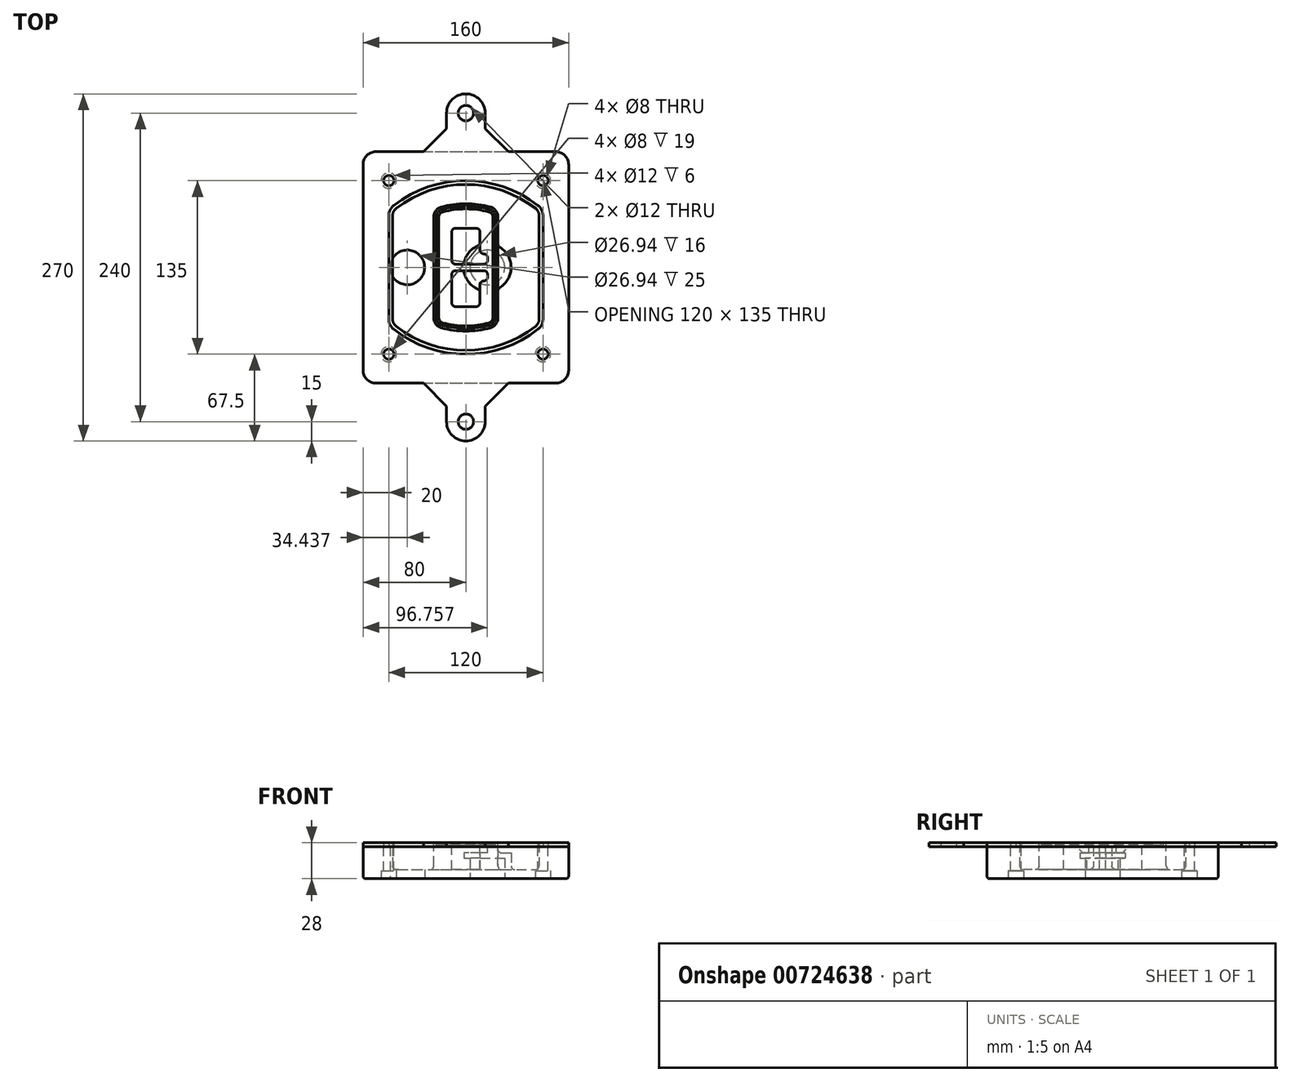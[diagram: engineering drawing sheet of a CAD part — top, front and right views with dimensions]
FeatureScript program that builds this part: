
annotation { "Feature Type Name" : "Feature", "Feature Type Description" : "" }
export const myFeature = defineFeature(function(context is Context, id is Id, definition is map)
    precondition{}
    {
        {
            var Q0;
            Q0=qCreatedBy(makeId("Top.planeOp"),FACE);
            var sketch = newSketch(context, id + "F0", { "sketchPlane" : qUnion([Q0])});
            skPoint(sketch, "E0.rect.middle", {"position": v(0, 0) * mm});
            skLineSegment(sketch, "E1.bottom", {"start": v(-70, -90) * mm, "end": v(70, -90) * mm});
            skLineSegment(sketch, "E1.top", {"start": v(-70, 90) * mm, "end": v(70, 90) * mm});
            skLineSegment(sketch, "E1.left", {"start": v(-80, -80) * mm, "end": v(-80, 80) * mm});
            skLineSegment(sketch, "E1.right", {"start": v(80, -80) * mm, "end": v(80, 80) * mm});
            skLineSegment(sketch, "E2", {"start": v(-80, 90) * mm, "end": v(80, -90) * mm, "construction": true});
            skLineSegment(sketch, "E3", {"start": v(80, 90) * mm, "end": v(-80, -90) * mm, "construction": true});
            skCircle(sketch, "E4", {"center": v(-60, 67.5) * mm, "radius": 4 * mm});
            skCircle(sketch, "E5", {"center": v(60, 67.5) * mm, "radius": 4 * mm});
            skCircle(sketch, "E6", {"center": v(60, -67.5) * mm, "radius": 4 * mm});
            skCircle(sketch, "E7", {"center": v(-60, -67.5) * mm, "radius": 4 * mm});
            skLineSegment(sketch, "E8", {"start": v(-60, 67.5) * mm, "end": v(60, 67.5) * mm, "construction": true});
            skLineSegment(sketch, "E9", {"start": v(60, 67.5) * mm, "end": v(60, -67.5) * mm, "construction": true});
            skLineSegment(sketch, "E10", {"start": v(60, -67.5) * mm, "end": v(-60, -67.5) * mm, "construction": true});
            skLineSegment(sketch, "E11", {"start": v(-60, -67.5) * mm, "end": v(-60, 67.5) * mm, "construction": true});
            skLineSegment(sketch, "E12", {"start": v(-60, 40.3) * mm, "end": v(-60, -40.3) * mm});
            skLineSegment(sketch, "E13", {"start": v(60, 40.3) * mm, "end": v(60, -40.3) * mm});
            skArc(sketch, "E14", {"start": v(56.15, 48.18) * mm, "mid": v(0, 67.5) * mm, "end": v(-56.15, 48.18) * mm});
            skArc(sketch, "E15", {"start": v(-56.15, -48.18) * mm, "mid": v(0, -67.5) * mm, "end": v(56.15, -48.18) * mm});
            skLineSegment(sketch, "E16", {"start": v(-60, 0) * mm, "end": v(60, 0) * mm, "construction": true});
            skPoint(sketch, "E17.visualSharp", {"position": v(-60, -45) * mm});
            skArc(sketch, "E17.filletArc", {"start": v(-60, -40.3) * mm, "mid": v(-58.99, -44.68) * mm, "end": v(-56.15, -48.18) * mm});
            skPoint(sketch, "E18.visualSharp", {"position": v(-60, 45) * mm});
            skArc(sketch, "E18.filletArc", {"start": v(-56.15, 48.18) * mm, "mid": v(-58.99, 44.68) * mm, "end": v(-60, 40.3) * mm});
            skPoint(sketch, "E19.visualSharp", {"position": v(60, 45) * mm});
            skArc(sketch, "E19.filletArc", {"start": v(60, 40.3) * mm, "mid": v(58.99, 44.68) * mm, "end": v(56.15, 48.18) * mm});
            skPoint(sketch, "E20.visualSharp", {"position": v(60, -45) * mm});
            skArc(sketch, "E20.filletArc", {"start": v(56.15, -48.18) * mm, "mid": v(58.99, -44.68) * mm, "end": v(60, -40.3) * mm});
            skPoint(sketch, "E21.visualSharp", {"position": v(-80, 90) * mm});
            skArc(sketch, "E21.filletArc", {"start": v(-70, 90) * mm, "mid": v(-77.07, 87.07) * mm, "end": v(-80, 80) * mm});
            skPoint(sketch, "E22.visualSharp", {"position": v(80, 90) * mm});
            skArc(sketch, "E22.filletArc", {"start": v(80, 80) * mm, "mid": v(77.07, 87.07) * mm, "end": v(70, 90) * mm});
            skPoint(sketch, "E23.visualSharp", {"position": v(80, -90) * mm});
            skArc(sketch, "E23.filletArc", {"start": v(70, -90) * mm, "mid": v(77.07, -87.07) * mm, "end": v(80, -80) * mm});
            skPoint(sketch, "E24.visualSharp", {"position": v(-80, -90) * mm});
            skArc(sketch, "E24.filletArc", {"start": v(-80, -80) * mm, "mid": v(-77.07, -87.07) * mm, "end": v(-70, -90) * mm});
            skArc(sketch, "E25.0", {"start": v(57, 40.3) * mm, "mid": v(56.3, 43.36) * mm, "end": v(54.3, 45.81) * mm});
            skLineSegment(sketch, "E25.1", {"start": v(57, 40.3) * mm, "end": v(57, -40.3) * mm});
            skArc(sketch, "E25.2", {"start": v(54.3, -45.81) * mm, "mid": v(56.3, -43.36) * mm, "end": v(57, -40.3) * mm});
            skArc(sketch, "E25.3", {"start": v(-54.3, -45.81) * mm, "mid": v(0, -64.5) * mm, "end": v(54.3, -45.81) * mm});
            skArc(sketch, "E25.4", {"start": v(-57, -40.3) * mm, "mid": v(-56.3, -43.36) * mm, "end": v(-54.3, -45.81) * mm});
            skArc(sketch, "E25.5", {"start": v(54.3, 45.81) * mm, "mid": v(0, 64.5) * mm, "end": v(-54.3, 45.81) * mm});
            skLineSegment(sketch, "E25.6", {"start": v(-57, 40.3) * mm, "end": v(-57, -40.3) * mm});
            skArc(sketch, "E25.7", {"start": v(-54.3, 45.81) * mm, "mid": v(-56.3, 43.36) * mm, "end": v(-57, 40.3) * mm});
            skArc(sketch, "E26.0", {"start": v(-58.62, 51.33) * mm, "mid": v(-62.58, 46.43) * mm, "end": v(-64, 40.3) * mm});
            skArc(sketch, "E26.1", {"start": v(58.62, 51.33) * mm, "mid": v(0, 71.5) * mm, "end": v(-58.62, 51.33) * mm});
            skArc(sketch, "E26.2", {"start": v(64, 40.3) * mm, "mid": v(62.58, 46.43) * mm, "end": v(58.62, 51.33) * mm});
            skLineSegment(sketch, "E26.3", {"start": v(64, 40.3) * mm, "end": v(64, -40.3) * mm});
            skArc(sketch, "E26.4", {"start": v(58.62, -51.33) * mm, "mid": v(62.58, -46.43) * mm, "end": v(64, -40.3) * mm});
            skLineSegment(sketch, "E26.5", {"start": v(-64, 40.3) * mm, "end": v(-64, -40.3) * mm});
            skArc(sketch, "E26.6", {"start": v(-58.62, -51.33) * mm, "mid": v(0, -71.5) * mm, "end": v(58.62, -51.33) * mm});
            skArc(sketch, "E26.7", {"start": v(-64, -40.3) * mm, "mid": v(-62.58, -46.43) * mm, "end": v(-58.62, -51.33) * mm});
            skSolve(sketch);
        }
        {
            var Q0;
            Q0=makeQuery(id+"F0.imprint","IMPRINT",FACE,{"disambiguationData":[TD([[makeQuery(id+"F0.imprint","IMPRINT",EDGE,{"derivedFrom":sQuery(id+"F0.wireOp",EDGE,"E1.bottom")}),1.0]])]});
            var Q1;
            Q1=makeQuery(id+"F0.imprint","IMPRINT",FACE,{"disambiguationData":[TD([[makeQuery(id+"F0.imprint","IMPRINT",EDGE,{"derivedFrom":sQuery(id+"F0.wireOp",EDGE,"E12")}),1.0]])]});
            var Q2;
            Q2=makeQuery(id+"F0.imprint","IMPRINT",FACE,{"disambiguationData":[TD([[makeQuery(id+"F0.imprint","IMPRINT",EDGE,{"derivedFrom":sQuery(id+"F0.wireOp",EDGE,"E25.0")}),1.0]])]});
            var Q3;
            Q3=makeQuery(id+"F0.imprint","IMPRINT",FACE,{"disambiguationData":[TD([[makeQuery(id+"F0.imprint","IMPRINT",EDGE,{"derivedFrom":sQuery(id+"F0.wireOp",EDGE,"E12")}),-1.0]])]});
            extrude(context, id + "F1", {"entities" : qUnion([Q0, Q1, Q2, Q3]), "oppositeDirection" : true, "depth" : 25 * mm});
        }
        {
            var Q0;
            Q0=makeQuery(id+"F0.imprint","IMPRINT",FACE,{"disambiguationData":[TD([[makeQuery(id+"F0.imprint","IMPRINT",EDGE,{"derivedFrom":sQuery(id+"F0.wireOp",EDGE,"E12")}),1.0]])]});
            extrude(context, id + "F2", {"entities" : qUnion([Q0]), "operationType" : NewBodyOperationType.ADD, "depth" : 3 * mm});
        }
        {
            var Q0;
            Q0=makeQuery(id+"F0.imprint","IMPRINT",FACE,{"disambiguationData":[TD([[makeQuery(id+"F0.imprint","IMPRINT",EDGE,{"derivedFrom":sQuery(id+"F0.wireOp",EDGE,"E25.0")}),1.0]])]});
            extrude(context, id + "F3", {"entities" : qUnion([Q0]), "operationType" : NewBodyOperationType.REMOVE, "oppositeDirection" : true, "depth" : 18 * mm});
        }
        {
            var Q0;
            Q0=makeQuery(id+"F2.opExtrude","CAP_FACE",FACE,{"disambiguationData":[OSD([sQuery(id+"F0.wireOp",EDGE,"E12"),sQuery(id+"F0.wireOp",EDGE,"E13"),sQuery(id+"F0.wireOp",EDGE,"E14"),sQuery(id+"F0.wireOp",EDGE,"E15"),sQuery(id+"F0.wireOp",EDGE,"E17.filletArc"),sQuery(id+"F0.wireOp",EDGE,"E18.filletArc"),sQuery(id+"F0.wireOp",EDGE,"E19.filletArc"),sQuery(id+"F0.wireOp",EDGE,"E20.filletArc"),sQuery(id+"F0.wireOp",EDGE,"E25.0"),sQuery(id+"F0.wireOp",EDGE,"E25.1"),sQuery(id+"F0.wireOp",EDGE,"E25.2"),sQuery(id+"F0.wireOp",EDGE,"E25.3"),sQuery(id+"F0.wireOp",EDGE,"E25.4"),sQuery(id+"F0.wireOp",EDGE,"E25.5"),sQuery(id+"F0.wireOp",EDGE,"E25.6"),sQuery(id+"F0.wireOp",EDGE,"E25.7")])],"isStart":false});
            var sketch = newSketch(context, id + "F4", { "sketchPlane" : qUnion([Q0])});
            skArc(sketch, "E27.0", {"start": v(-19.08, -46.97) * mm, "mid": v(0, -49.5) * mm, "end": v(19.08, -46.97) * mm});
            skArc(sketch, "E28.0", {"start": v(19.08, 46.97) * mm, "mid": v(0, 49.5) * mm, "end": v(-19.08, 46.97) * mm});
            skLineSegment(sketch, "E29", {"start": v(-25, 39.25) * mm, "end": v(-25, -39.25) * mm});
            skLineSegment(sketch, "E30", {"start": v(25, 39.25) * mm, "end": v(25, -39.25) * mm});
            skLineSegment(sketch, "E31", {"start": v(-25, 45.1) * mm, "end": v(25, 45.1) * mm, "construction": true});
            skLineSegment(sketch, "E32", {"start": v(-25, -45.1) * mm, "end": v(25, -45.1) * mm, "construction": true});
            skPoint(sketch, "E33.visualSharp", {"position": v(-25, 45.1) * mm});
            skArc(sketch, "E33.filletArc", {"start": v(-19.08, 46.97) * mm, "mid": v(-23.35, 44.11) * mm, "end": v(-25, 39.25) * mm});
            skPoint(sketch, "E34.visualSharp", {"position": v(25, 45.1) * mm});
            skArc(sketch, "E34.filletArc", {"start": v(25, 39.25) * mm, "mid": v(23.35, 44.11) * mm, "end": v(19.08, 46.97) * mm});
            skPoint(sketch, "E35.visualSharp", {"position": v(25, -45.1) * mm});
            skArc(sketch, "E35.filletArc", {"start": v(19.08, -46.97) * mm, "mid": v(23.35, -44.11) * mm, "end": v(25, -39.25) * mm});
            skPoint(sketch, "E36.visualSharp", {"position": v(-25, -45.1) * mm});
            skArc(sketch, "E36.filletArc", {"start": v(-25, -39.25) * mm, "mid": v(-23.35, -44.11) * mm, "end": v(-19.08, -46.97) * mm});
            skArc(sketch, "E37.0", {"start": v(54.3, 45.81) * mm, "mid": v(0, 64.5) * mm, "end": v(-54.3, 45.81) * mm});
            skArc(sketch, "E37.1", {"start": v(-54.3, 45.81) * mm, "mid": v(-56.3, 43.36) * mm, "end": v(-57, 40.3) * mm});
            skLineSegment(sketch, "E37.2", {"start": v(-57, 40.3) * mm, "end": v(-57, -40.3) * mm});
            skArc(sketch, "E37.3", {"start": v(-57, -40.3) * mm, "mid": v(-56.3, -43.36) * mm, "end": v(-54.3, -45.81) * mm});
            skArc(sketch, "E37.4", {"start": v(-54.3, -45.81) * mm, "mid": v(0, -64.5) * mm, "end": v(54.3, -45.81) * mm});
            skArc(sketch, "E37.5", {"start": v(54.3, -45.81) * mm, "mid": v(56.3, -43.36) * mm, "end": v(57, -40.3) * mm});
            skLineSegment(sketch, "E37.6", {"start": v(57, 40.3) * mm, "end": v(57, -40.3) * mm});
            skArc(sketch, "E37.7", {"start": v(57, 40.3) * mm, "mid": v(56.3, 43.36) * mm, "end": v(54.3, 45.81) * mm});
            skLineSegment(sketch, "E38.0", {"start": v(23, 39.25) * mm, "end": v(23, -39.25) * mm});
            skArc(sketch, "E38.1", {"start": v(18.56, -45.04) * mm, "mid": v(21.76, -42.9) * mm, "end": v(23, -39.25) * mm});
            skArc(sketch, "E38.2", {"start": v(-18.56, -45.04) * mm, "mid": v(0, -47.5) * mm, "end": v(18.56, -45.04) * mm});
            skArc(sketch, "E38.3", {"start": v(-23, -39.25) * mm, "mid": v(-21.76, -42.9) * mm, "end": v(-18.56, -45.04) * mm});
            skLineSegment(sketch, "E38.4", {"start": v(-23, 39.25) * mm, "end": v(-23, -39.25) * mm});
            skArc(sketch, "E38.5", {"start": v(23, 39.25) * mm, "mid": v(21.76, 42.9) * mm, "end": v(18.56, 45.04) * mm});
            skArc(sketch, "E38.6", {"start": v(-18.56, 45.04) * mm, "mid": v(-21.76, 42.9) * mm, "end": v(-23, 39.25) * mm});
            skArc(sketch, "E38.7", {"start": v(18.56, 45.04) * mm, "mid": v(0, 47.5) * mm, "end": v(-18.56, 45.04) * mm});
            skArc(sketch, "E39.0", {"start": v(21, 39.25) * mm, "mid": v(20.18, 41.68) * mm, "end": v(18.04, 43.1) * mm});
            skLineSegment(sketch, "E39.1", {"start": v(21, 39.25) * mm, "end": v(21, -39.25) * mm});
            skArc(sketch, "E39.2", {"start": v(18.04, -43.1) * mm, "mid": v(20.18, -41.68) * mm, "end": v(21, -39.25) * mm});
            skArc(sketch, "E39.3", {"start": v(-18.04, -43.1) * mm, "mid": v(0, -45.5) * mm, "end": v(18.04, -43.1) * mm});
            skArc(sketch, "E39.4", {"start": v(-21, -39.25) * mm, "mid": v(-20.18, -41.68) * mm, "end": v(-18.04, -43.1) * mm});
            skArc(sketch, "E39.5", {"start": v(18.04, 43.1) * mm, "mid": v(0, 45.5) * mm, "end": v(-18.04, 43.1) * mm});
            skLineSegment(sketch, "E39.6", {"start": v(-21, 39.25) * mm, "end": v(-21, -39.25) * mm});
            skArc(sketch, "E39.7", {"start": v(-18.04, 43.1) * mm, "mid": v(-20.18, 41.68) * mm, "end": v(-21, 39.25) * mm});
            skLineSegment(sketch, "E40", {"start": v(-25, 0) * mm, "end": v(25, 0) * mm, "construction": true});
            skLineSegment(sketch, "E41", {"start": v(-11, 5.5) * mm, "end": v(-11, 27.5) * mm});
            skLineSegment(sketch, "E42", {"start": v(-8, 30.5) * mm, "end": v(8, 30.5) * mm});
            skLineSegment(sketch, "E43", {"start": v(11, 27.5) * mm, "end": v(11, 13.5) * mm});
            skLineSegment(sketch, "E44", {"start": v(14, 10.5) * mm, "end": v(14, 10.5) * mm});
            skLineSegment(sketch, "E45", {"start": v(17, 7.5) * mm, "end": v(17, 5.5) * mm});
            skLineSegment(sketch, "E46", {"start": v(14, 2.5) * mm, "end": v(-8, 2.5) * mm});
            skPoint(sketch, "E47.visualSharp", {"position": v(-11, 30.5) * mm});
            skArc(sketch, "E47.filletArc", {"start": v(-8, 30.5) * mm, "mid": v(-10.12, 29.62) * mm, "end": v(-11, 27.5) * mm});
            skPoint(sketch, "E48.visualSharp", {"position": v(11, 30.5) * mm});
            skArc(sketch, "E48.filletArc", {"start": v(11, 27.5) * mm, "mid": v(10.12, 29.62) * mm, "end": v(8, 30.5) * mm});
            skPoint(sketch, "E49.visualSharp", {"position": v(11, 10.5) * mm});
            skArc(sketch, "E49.filletArc", {"start": v(11, 13.5) * mm, "mid": v(11.88, 11.38) * mm, "end": v(14, 10.5) * mm});
            skPoint(sketch, "E50.visualSharp", {"position": v(17, 10.5) * mm});
            skArc(sketch, "E50.filletArc", {"start": v(17, 7.5) * mm, "mid": v(16.12, 9.62) * mm, "end": v(14, 10.5) * mm});
            skPoint(sketch, "E51.visualSharp", {"position": v(17, 2.5) * mm});
            skArc(sketch, "E51.filletArc", {"start": v(14, 2.5) * mm, "mid": v(16.12, 3.38) * mm, "end": v(17, 5.5) * mm});
            skPoint(sketch, "E52.visualSharp", {"position": v(-11, 2.5) * mm});
            skArc(sketch, "E52.filletArc", {"start": v(-11, 5.5) * mm, "mid": v(-10.12, 3.38) * mm, "end": v(-8, 2.5) * mm});
            skLineSegment(sketch, "E53.0.MirrorCS", {"start": v(14, -2.5) * mm, "end": v(-8, -2.5) * mm});
            skArc(sketch, "E54.0.MirrorCS", {"start": v(-11, -5.5) * mm, "mid": v(-10.12, -3.38) * mm, "end": v(-8, -2.5) * mm});
            skLineSegment(sketch, "E55.0.MirrorCS", {"start": v(-11, -5.5) * mm, "end": v(-11, -27.5) * mm});
            skArc(sketch, "E56.0.MirrorCS", {"start": v(-8, -30.5) * mm, "mid": v(-10.12, -29.62) * mm, "end": v(-11, -27.5) * mm});
            skLineSegment(sketch, "E57.0.MirrorCS", {"start": v(-8, -30.5) * mm, "end": v(8, -30.5) * mm});
            skArc(sketch, "E58.0.MirrorCS", {"start": v(11, -27.5) * mm, "mid": v(10.12, -29.62) * mm, "end": v(8, -30.5) * mm});
            skLineSegment(sketch, "E59.0.MirrorCS", {"start": v(11, -27.5) * mm, "end": v(11, -13.5) * mm});
            skArc(sketch, "E60.0.MirrorCS", {"start": v(11, -13.5) * mm, "mid": v(11.88, -11.38) * mm, "end": v(14, -10.5) * mm});
            skArc(sketch, "E61.0.MirrorCS", {"start": v(17, -7.5) * mm, "mid": v(16.12, -9.62) * mm, "end": v(14, -10.5) * mm});
            skLineSegment(sketch, "E62.0.MirrorCS", {"start": v(17, -7.5) * mm, "end": v(17, -5.5) * mm});
            skArc(sketch, "E63.0.MirrorCS", {"start": v(14, -2.5) * mm, "mid": v(16.12, -3.38) * mm, "end": v(17, -5.5) * mm});
            skSolve(sketch);
        }
        {
            var Q0;
            Q0=makeQuery(id+"F4.imprint","IMPRINT",FACE,{"disambiguationData":[TD([[makeQuery(id+"F4.imprint","IMPRINT",EDGE,{"derivedFrom":sQuery(id+"F4.wireOp",EDGE,"E27.0")}),1.0]])]});
            var Q1;
            Q1=makeQuery(id+"F4.imprint","IMPRINT",FACE,{"disambiguationData":[TD([[makeQuery(id+"F4.imprint","IMPRINT",EDGE,{"derivedFrom":sQuery(id+"F4.wireOp",EDGE,"E38.0")}),-1.0]])]});
            var Q2;
            Q2=makeQuery(id+"F4.imprint","IMPRINT",FACE,{"disambiguationData":[TD([[makeQuery(id+"F4.imprint","IMPRINT",EDGE,{"derivedFrom":sQuery(id+"F4.wireOp",EDGE,"E39.0")}),1.0]])]});
            extrude(context, id + "F5", {"entities" : qUnion([Q0, Q1, Q2]), "operationType" : NewBodyOperationType.ADD, "endBound" : BoundingType.UP_TO_NEXT, "oppositeDirection" : true, "depth" : 25 * mm});
        }
        {
            var Q0;
            Q0=makeQuery(id+"F4.imprint","IMPRINT",FACE,{"disambiguationData":[TD([[makeQuery(id+"F4.imprint","IMPRINT",EDGE,{"derivedFrom":sQuery(id+"F4.wireOp",EDGE,"E38.0")}),-1.0]])]});
            extrude(context, id + "F6", {"entities" : qUnion([Q0]), "operationType" : NewBodyOperationType.REMOVE, "oppositeDirection" : true, "depth" : 2 * mm});
        }
        {
            var Q0;
            Q0=makeQuery(id+"F1.opExtrude","CAP_FACE",FACE,{"disambiguationData":[OSD([sQuery(id+"F0.wireOp",EDGE,"E1.bottom"),sQuery(id+"F0.wireOp",EDGE,"E1.top"),sQuery(id+"F0.wireOp",EDGE,"E1.left"),sQuery(id+"F0.wireOp",EDGE,"E1.right"),sQuery(id+"F0.wireOp",EDGE,"E4"),sQuery(id+"F0.wireOp",EDGE,"E5"),sQuery(id+"F0.wireOp",EDGE,"E6"),sQuery(id+"F0.wireOp",EDGE,"E7"),sQuery(id+"F0.wireOp",EDGE,"E21.filletArc"),sQuery(id+"F0.wireOp",EDGE,"E22.filletArc"),sQuery(id+"F0.wireOp",EDGE,"E23.filletArc"),sQuery(id+"F0.wireOp",EDGE,"E24.filletArc")])],"isStart":false});
            var sketch = newSketch(context, id + "F7", { "sketchPlane" : qUnion([Q0])});
            skCircle(sketch, "E64", {"center": v(16.76, 0) * mm, "radius": 13.47 * mm});
            skCircle(sketch, "E65", {"center": v(-45.56, 0) * mm, "radius": 13.47 * mm});
            skLineSegment(sketch, "E66", {"start": v(80, 0) * mm, "end": v(-80, 0) * mm});
            skCircle(sketch, "E67", {"center": v(16.76, 0) * mm, "radius": 18.47 * mm});
            skCircle(sketch, "E68", {"center": v(60, -67.5) * mm, "radius": 6 * mm});
            skCircle(sketch, "E69", {"center": v(-60, -67.5) * mm, "radius": 6 * mm});
            skCircle(sketch, "E70", {"center": v(-60, 67.5) * mm, "radius": 6 * mm});
            skCircle(sketch, "E71", {"center": v(60, 67.5) * mm, "radius": 6 * mm});
            skSolve(sketch);
        }
        {
            var Q0;
            {var subQ1=sQuery(id+"F7.wireOp",EDGE,"E66");var subQ4=sQuery(id+"F7.wireOp",EDGE,"E64");var subQ6=makeQuery(id+"F7.imprint","INTERSECT",VERTEX,{"disambiguationData":[OD(0.0)],"derivedFrom":[subQ4,subQ1]});Q0=makeQuery(id+"F7.imprint","IMPRINT",FACE,{"disambiguationData":[TD([[makeQuery(id+"F7.imprint","IMPRINT",EDGE,{"disambiguationData":[TD([[subQ6,-1.0]])],"derivedFrom":subQ4}),-1.0]])]});}
            var Q1;
            {var subQ0=sQuery(id+"F7.wireOp",EDGE,"E66");var subQ1=sQuery(id+"F7.wireOp",EDGE,"E64");var subQ3=makeQuery(id+"F7.imprint","INTERSECT",VERTEX,{"disambiguationData":[OD(0.0)],"derivedFrom":[subQ1,subQ0]});Q1=makeQuery(id+"F7.imprint","IMPRINT",FACE,{"disambiguationData":[TD([[makeQuery(id+"F7.imprint","IMPRINT",EDGE,{"disambiguationData":[TD([[subQ3,-1.0]])],"derivedFrom":subQ1}),1.0]])]});}
            var Q2;
            {var subQ0=sQuery(id+"F7.wireOp",EDGE,"E66");var subQ1=sQuery(id+"F7.wireOp",EDGE,"E64");var subQ3=makeQuery(id+"F7.imprint","INTERSECT",VERTEX,{"disambiguationData":[OD(0.0)],"derivedFrom":[subQ1,subQ0]});Q2=makeQuery(id+"F7.imprint","IMPRINT",FACE,{"disambiguationData":[TD([[makeQuery(id+"F7.imprint","IMPRINT",EDGE,{"disambiguationData":[TD([[subQ3,1.0]])],"derivedFrom":subQ1}),1.0]])]});}
            var Q3;
            {var subQ1=sQuery(id+"F7.wireOp",EDGE,"E66");var subQ4=sQuery(id+"F7.wireOp",EDGE,"E64");var subQ6=makeQuery(id+"F7.imprint","INTERSECT",VERTEX,{"disambiguationData":[OD(0.0)],"derivedFrom":[subQ4,subQ1]});Q3=makeQuery(id+"F7.imprint","IMPRINT",FACE,{"disambiguationData":[TD([[makeQuery(id+"F7.imprint","IMPRINT",EDGE,{"disambiguationData":[TD([[subQ6,1.0]])],"derivedFrom":subQ4}),-1.0]])]});}
            extrude(context, id + "F8", {"entities" : qUnion([Q0, Q1, Q2, Q3]), "operationType" : NewBodyOperationType.ADD, "oppositeDirection" : true, "depth" : 20 * mm});
        }
        {
            var Q0;
            {var subQ0=sQuery(id+"F7.wireOp",EDGE,"E66");var subQ1=sQuery(id+"F7.wireOp",EDGE,"E64");var subQ3=makeQuery(id+"F7.imprint","INTERSECT",VERTEX,{"disambiguationData":[OD(0.0)],"derivedFrom":[subQ1,subQ0]});Q0=makeQuery(id+"F7.imprint","IMPRINT",FACE,{"disambiguationData":[TD([[makeQuery(id+"F7.imprint","IMPRINT",EDGE,{"disambiguationData":[TD([[subQ3,-1.0]])],"derivedFrom":subQ1}),1.0]])]});}
            var Q1;
            {var subQ0=sQuery(id+"F7.wireOp",EDGE,"E66");var subQ1=sQuery(id+"F7.wireOp",EDGE,"E64");var subQ3=makeQuery(id+"F7.imprint","INTERSECT",VERTEX,{"disambiguationData":[OD(0.0)],"derivedFrom":[subQ1,subQ0]});Q1=makeQuery(id+"F7.imprint","IMPRINT",FACE,{"disambiguationData":[TD([[makeQuery(id+"F7.imprint","IMPRINT",EDGE,{"disambiguationData":[TD([[subQ3,1.0]])],"derivedFrom":subQ1}),1.0]])]});}
            extrude(context, id + "F9", {"entities" : qUnion([Q0, Q1]), "operationType" : NewBodyOperationType.REMOVE, "oppositeDirection" : true, "depth" : 16 * mm});
        }
        {
            var Q0;
            {var subQ0=sQuery(id+"F7.wireOp",EDGE,"E66");var subQ1=sQuery(id+"F7.wireOp",EDGE,"E65");var subQ3=makeQuery(id+"F7.imprint","INTERSECT",VERTEX,{"disambiguationData":[OD(0.0)],"derivedFrom":[subQ1,subQ0]});Q0=makeQuery(id+"F7.imprint","IMPRINT",FACE,{"disambiguationData":[TD([[makeQuery(id+"F7.imprint","IMPRINT",EDGE,{"disambiguationData":[TD([[subQ3,-1.0]])],"derivedFrom":subQ1}),1.0]])]});}
            var Q1;
            {var subQ0=sQuery(id+"F7.wireOp",EDGE,"E66");var subQ1=sQuery(id+"F7.wireOp",EDGE,"E65");var subQ3=makeQuery(id+"F7.imprint","INTERSECT",VERTEX,{"disambiguationData":[OD(0.0)],"derivedFrom":[subQ1,subQ0]});Q1=makeQuery(id+"F7.imprint","IMPRINT",FACE,{"disambiguationData":[TD([[makeQuery(id+"F7.imprint","IMPRINT",EDGE,{"disambiguationData":[TD([[subQ3,1.0]])],"derivedFrom":subQ1}),1.0]])]});}
            extrude(context, id + "F10", {"entities" : qUnion([Q0, Q1]), "operationType" : NewBodyOperationType.REMOVE, "oppositeDirection" : true, "depth" : 25 * mm});
        }
        {
            var Q0;
            Q0=makeQuery(id+"F7.imprint","IMPRINT",FACE,{"disambiguationData":[TD([[makeQuery(id+"F7.imprint","IMPRINT",EDGE,{"derivedFrom":sQuery(id+"F7.wireOp",EDGE,"E68")}),1.0]])]});
            var Q1;
            Q1=makeQuery(id+"F7.imprint","IMPRINT",FACE,{"disambiguationData":[TD([[makeQuery(id+"F7.imprint","IMPRINT",EDGE,{"derivedFrom":makeQuery(id+"F1.opExtrude","CAP_EDGE",EDGE,{"disambiguationData":[OSD([sQuery(id+"F0.wireOp",EDGE,"E5")])],"isStart":false})}),-1.0]])]});
            var Q2;
            Q2=makeQuery(id+"F7.imprint","IMPRINT",FACE,{"disambiguationData":[TD([[makeQuery(id+"F7.imprint","IMPRINT",EDGE,{"derivedFrom":sQuery(id+"F7.wireOp",EDGE,"E69")}),1.0]])]});
            var Q3;
            Q3=makeQuery(id+"F7.imprint","IMPRINT",FACE,{"disambiguationData":[TD([[makeQuery(id+"F7.imprint","IMPRINT",EDGE,{"derivedFrom":makeQuery(id+"F1.opExtrude","CAP_EDGE",EDGE,{"disambiguationData":[OSD([sQuery(id+"F0.wireOp",EDGE,"E4")])],"isStart":false})}),-1.0]])]});
            var Q4;
            Q4=makeQuery(id+"F7.imprint","IMPRINT",FACE,{"disambiguationData":[TD([[makeQuery(id+"F7.imprint","IMPRINT",EDGE,{"derivedFrom":sQuery(id+"F7.wireOp",EDGE,"E70")}),1.0]])]});
            var Q5;
            Q5=makeQuery(id+"F7.imprint","IMPRINT",FACE,{"disambiguationData":[TD([[makeQuery(id+"F7.imprint","IMPRINT",EDGE,{"derivedFrom":makeQuery(id+"F1.opExtrude","CAP_EDGE",EDGE,{"disambiguationData":[OSD([sQuery(id+"F0.wireOp",EDGE,"E7")])],"isStart":false})}),-1.0]])]});
            var Q6;
            Q6=makeQuery(id+"F7.imprint","IMPRINT",FACE,{"disambiguationData":[TD([[makeQuery(id+"F7.imprint","IMPRINT",EDGE,{"derivedFrom":sQuery(id+"F7.wireOp",EDGE,"E71")}),1.0]])]});
            var Q7;
            Q7=makeQuery(id+"F7.imprint","IMPRINT",FACE,{"disambiguationData":[TD([[makeQuery(id+"F7.imprint","IMPRINT",EDGE,{"derivedFrom":makeQuery(id+"F1.opExtrude","CAP_EDGE",EDGE,{"disambiguationData":[OSD([sQuery(id+"F0.wireOp",EDGE,"E6")])],"isStart":false})}),-1.0]])]});
            extrude(context, id + "F11", {"entities" : qUnion([Q0, Q1, Q2, Q3, Q4, Q5, Q6, Q7]), "operationType" : NewBodyOperationType.REMOVE, "oppositeDirection" : true, "depth" : 6 * mm});
        }
        {
            var Q0;
            Q0=makeQuery(id+"F9.boolean.opBoolean","COPY",FACE,{"derivedFrom":makeQuery(id+"F9.opExtrude","CAP_FACE",FACE,{"disambiguationData":[OSD([sQuery(id+"F7.wireOp",EDGE,"E64")])],"isStart":false})});
            var sketch = newSketch(context, id + "F12", { "sketchPlane" : qUnion([Q0])});
            skArc(sketch, "E72.0", {"start": v(11, 17.55) * mm, "mid": v(2.57, 11.82) * mm, "end": v(-1.54, 2.5) * mm});
            skArc(sketch, "E72.1", {"start": v(-1.54, -2.5) * mm, "mid": v(2.57, -11.82) * mm, "end": v(11, -17.55) * mm});
            skLineSegment(sketch, "E73", {"start": v(-1.54, -2.5) * mm, "end": v(14, -2.5) * mm});
            skLineSegment(sketch, "E74.0", {"start": v(14, 2.5) * mm, "end": v(-1.54, 2.5) * mm});
            skArc(sketch, "E74.1", {"start": v(14, 2.5) * mm, "mid": v(16.12, 3.38) * mm, "end": v(17, 5.5) * mm});
            skLineSegment(sketch, "E74.2", {"start": v(17, 7.5) * mm, "end": v(17, 5.5) * mm});
            skArc(sketch, "E74.3", {"start": v(17, 7.5) * mm, "mid": v(16.12, 9.62) * mm, "end": v(14, 10.5) * mm});
            skArc(sketch, "E74.4", {"start": v(11, 13.5) * mm, "mid": v(11.88, 11.38) * mm, "end": v(14, 10.5) * mm});
            skLineSegment(sketch, "E74.5", {"start": v(11, 17.55) * mm, "end": v(11, 13.5) * mm});
            skLineSegment(sketch, "E74.7", {"start": v(14, -2.5) * mm, "end": v(-1.54, -2.5) * mm});
            skArc(sketch, "E74.8", {"start": v(14, -2.5) * mm, "mid": v(16.12, -3.38) * mm, "end": v(17, -5.5) * mm});
            skLineSegment(sketch, "E74.9", {"start": v(17, -7.5) * mm, "end": v(17, -5.5) * mm});
            skArc(sketch, "E74.10", {"start": v(17, -7.5) * mm, "mid": v(16.12, -9.62) * mm, "end": v(14, -10.5) * mm});
            skArc(sketch, "E74.11", {"start": v(11, -13.5) * mm, "mid": v(11.88, -11.38) * mm, "end": v(14, -10.5) * mm});
            skLineSegment(sketch, "E74.12", {"start": v(11, -17.55) * mm, "end": v(11, -13.5) * mm});
            skPoint(sketch, "E75.orphan", {"position": v(11, -27.5) * mm});
            skPoint(sketch, "E76.orphan", {"position": v(-8, -2.5) * mm});
            skPoint(sketch, "E77.orphan", {"position": v(-8, 2.5) * mm});
            skPoint(sketch, "E78.orphan", {"position": v(11, 27.5) * mm});
            skSolve(sketch);
        }
        {
            var Q0;
            {var subQ7=sQuery(id+"F12.wireOp",EDGE,"E72.0");var subQ14=sQuery(id+"F12.wireOp",EDGE,"E72.1");var subQ16=sQuery(id+"F12.wireOp",EDGE,"E74.1");var subQ18=sQuery(id+"F12.wireOp",EDGE,"E74.8");Q0=qUnion([makeQuery(id+"F12.imprint","IMPRINT",FACE,{"disambiguationData":[TD([[makeQuery(id+"F12.imprint","IMPRINT",EDGE,{"derivedFrom":subQ7}),1.0]])]}),makeQuery(id+"F12.imprint","IMPRINT",FACE,{"disambiguationData":[TD([[makeQuery(id+"F12.imprint","IMPRINT",EDGE,{"derivedFrom":subQ14}),1.0]])]}),makeQuery(id+"F12.imprint","IMPRINT",FACE,{"disambiguationData":[TD([[makeQuery(id+"F12.imprint","IMPRINT",EDGE,{"derivedFrom":subQ16}),1.0]])]}),makeQuery(id+"F12.imprint","IMPRINT",FACE,{"disambiguationData":[TD([[makeQuery(id+"F12.imprint","IMPRINT",EDGE,{"derivedFrom":subQ18}),-1.0]])]})]);}
            var Q1;
            Q1=makeQuery(id+"F5.boolean.opBoolean","SPLIT",FACE,{"disambiguationData":[TD([makeQuery(id+"F5.opExtrude","SWEPT_FACE",FACE,{"disambiguationData":[OSD([sQuery(id+"F4.wireOp",EDGE,"E41")])]})])],"derivedFrom":makeQuery(id+"F3.boolean.opBoolean","COPY",FACE,{"derivedFrom":makeQuery(id+"F3.opExtrude","CAP_FACE",FACE,{"disambiguationData":[OSD([sQuery(id+"F0.wireOp",EDGE,"E25.0"),sQuery(id+"F0.wireOp",EDGE,"E25.1"),sQuery(id+"F0.wireOp",EDGE,"E25.2"),sQuery(id+"F0.wireOp",EDGE,"E25.3"),sQuery(id+"F0.wireOp",EDGE,"E25.4"),sQuery(id+"F0.wireOp",EDGE,"E25.5"),sQuery(id+"F0.wireOp",EDGE,"E25.6"),sQuery(id+"F0.wireOp",EDGE,"E25.7")])],"isStart":false})})});
            extrude(context, id + "F13", {"entities" : qUnion([Q0]), "operationType" : NewBodyOperationType.REMOVE, "endBound" : BoundingType.UP_TO_SURFACE, "endBoundEntityFace" : qUnion([Q1]), "depth" : 25 * mm});
        }
        {
            var Q0;
            Q0=makeQuery(id+"F3.boolean.opBoolean","COPY",EDGE,{"derivedFrom":makeQuery(id+"F3.opExtrude","CAP_EDGE",EDGE,{"disambiguationData":[OSD([sQuery(id+"F0.wireOp",EDGE,"E25.6")])],"isStart":false})});
            var Q1;
            Q1=makeQuery(id+"F8.boolean.opBoolean","INTERSECT",EDGE,{"derivedFrom":[makeQuery(id+"F5.opExtrude","SWEPT_FACE",FACE,{"disambiguationData":[OSD([sQuery(id+"F4.wireOp",EDGE,"E30")])]}),makeQuery(id+"F8.opExtrude","CAP_FACE",FACE,{"disambiguationData":[OSD([sQuery(id+"F7.wireOp",EDGE,"E67")])],"isStart":false})]});
            var Q2;
            Q2=makeQuery(id+"F8.boolean.opBoolean","INTERSECT",EDGE,{"disambiguationData":[OD(1.0)],"derivedFrom":[makeQuery(id+"F5.opExtrude","SWEPT_FACE",FACE,{"disambiguationData":[OSD([sQuery(id+"F4.wireOp",EDGE,"E30")])]}),makeQuery(id+"F8.opExtrude","SWEPT_FACE",FACE,{"disambiguationData":[OSD([sQuery(id+"F7.wireOp",EDGE,"E67")])]})]});
            var Q3;
            {var subQ0=sQuery(id+"F4.wireOp",EDGE,"E30");Q3=makeQuery(id+"F8.boolean.opBoolean","SPLIT",EDGE,{"disambiguationData":[TD([makeQuery(id+"F5.opExtrude","SWEPT_FACE",FACE,{"disambiguationData":[OSD([sQuery(id+"F4.wireOp",EDGE,"E35.filletArc")])]})])],"derivedFrom":makeQuery(id+"F5.opExtrude","CAP_EDGE",EDGE,{"disambiguationData":[OSD([subQ0])],"isStart":false})});}
            var Q4;
            {var subQ0=sQuery(id+"F0.wireOp",EDGE,"E25.7");var subQ1=sQuery(id+"F0.wireOp",EDGE,"E25.1");var subQ2=sQuery(id+"F0.wireOp",EDGE,"E25.6");var subQ3=sQuery(id+"F0.wireOp",EDGE,"E25.5");var subQ4=sQuery(id+"F0.wireOp",EDGE,"E25.4");var subQ5=sQuery(id+"F0.wireOp",EDGE,"E25.0");var subQ6=sQuery(id+"F0.wireOp",EDGE,"E25.2");var subQ7=sQuery(id+"F0.wireOp",EDGE,"E25.3");Q4=makeQuery(id+"F8.boolean.opBoolean","INTERSECT",EDGE,{"derivedFrom":[makeQuery(id+"F5.boolean.opBoolean","SPLIT",FACE,{"disambiguationData":[TD([makeQuery(id+"F2.opExtrude","SWEPT_FACE",FACE,{"disambiguationData":[OSD([subQ5])]})])],"derivedFrom":makeQuery(id+"F3.boolean.opBoolean","COPY",FACE,{"derivedFrom":makeQuery(id+"F3.opExtrude","CAP_FACE",FACE,{"disambiguationData":[OSD([subQ5,subQ1,subQ6,subQ7,subQ4,subQ3,subQ2,subQ0])],"isStart":false})})}),makeQuery(id+"F8.opExtrude","SWEPT_FACE",FACE,{"disambiguationData":[OSD([sQuery(id+"F7.wireOp",EDGE,"E67")])]})]});}
            var Q5;
            Q5=makeQuery(id+"F8.boolean.opBoolean","INTERSECT",EDGE,{"disambiguationData":[OD(0.0)],"derivedFrom":[makeQuery(id+"F5.opExtrude","SWEPT_FACE",FACE,{"disambiguationData":[OSD([sQuery(id+"F4.wireOp",EDGE,"E30")])]}),makeQuery(id+"F8.opExtrude","SWEPT_FACE",FACE,{"disambiguationData":[OSD([sQuery(id+"F7.wireOp",EDGE,"E67")])]})]});
            fillet(context, id + "F14", {"entities" : qUnion([Q0, Q1, Q2, Q3, Q4, Q5]), "radius" : 3 * mm, "tangentPropagation" : true, "allowEdgeOverflow" : false});
        }
        {
            var Q0;
            Q0=makeQuery(id+"F1.opExtrude","CAP_EDGE",EDGE,{"disambiguationData":[OSD([sQuery(id+"F0.wireOp",EDGE,"E1.bottom")])],"isStart":false});
            fillet(context, id + "F15", {"entities" : qUnion([Q0]), "radius" : 2 * mm, "tangentPropagation" : true, "allowEdgeOverflow" : false});
        }
        {
            var Q0;
            {var subQ0=sQuery(id+"F0.wireOp",EDGE,"E21.filletArc");var subQ1=sQuery(id+"F0.wireOp",EDGE,"E7");var subQ2=sQuery(id+"F0.wireOp",EDGE,"E6");var subQ3=sQuery(id+"F0.wireOp",EDGE,"E5");var subQ4=sQuery(id+"F0.wireOp",EDGE,"E4");var subQ5=sQuery(id+"F0.wireOp",EDGE,"E22.filletArc");var subQ6=sQuery(id+"F0.wireOp",EDGE,"E1.bottom");var subQ7=sQuery(id+"F0.wireOp",EDGE,"E1.right");var subQ8=sQuery(id+"F0.wireOp",EDGE,"E1.top");var subQ9=sQuery(id+"F0.wireOp",EDGE,"E1.left");var subQ10=sQuery(id+"F0.wireOp",EDGE,"E23.filletArc");var subQ11=sQuery(id+"F0.wireOp",EDGE,"E24.filletArc");Q0=makeQuery(id+"F2.boolean.opBoolean","SPLIT",FACE,{"disambiguationData":[TD([makeQuery(id+"F1.opExtrude","SWEPT_FACE",FACE,{"disambiguationData":[OSD([subQ6])]})])],"derivedFrom":makeQuery(id+"F1.opExtrude","CAP_FACE",FACE,{"disambiguationData":[OSD([subQ6,subQ8,subQ9,subQ7,subQ4,subQ3,subQ2,subQ1,subQ0,subQ5,subQ10,subQ11])],"isStart":true})});}
            var sketch = newSketch(context, id + "F16", { "sketchPlane" : qUnion([Q0])});
            skLineSegment(sketch, "E79", {"start": v(0, 90) * mm, "end": v(0, 120) * mm, "construction": true});
            skCircle(sketch, "E80", {"center": v(0, 120) * mm, "radius": 6 * mm});
            skLineSegment(sketch, "E81", {"start": v(-33, 90) * mm, "end": v(-15, 108) * mm});
            skLineSegment(sketch, "E82", {"start": v(-15, 108) * mm, "end": v(-15, 120) * mm});
            skLineSegment(sketch, "E83", {"start": v(33, 90) * mm, "end": v(15, 108) * mm});
            skLineSegment(sketch, "E84", {"start": v(15, 108) * mm, "end": v(15, 120) * mm});
            skArc(sketch, "E85", {"start": v(15, 120) * mm, "mid": v(0, 135) * mm, "end": v(-15, 120) * mm});
            skLineSegment(sketch, "E86", {"start": v(-80, 0) * mm, "end": v(80, 0) * mm, "construction": true});
            skLineSegment(sketch, "E87.MirrorCS", {"start": v(33, -90) * mm, "end": v(15, -108) * mm});
            skLineSegment(sketch, "E88.MirrorCS", {"start": v(15, -108) * mm, "end": v(15, -120) * mm});
            skArc(sketch, "E89.MirrorCS", {"start": v(15, -120) * mm, "mid": v(0, -135) * mm, "end": v(-15, -120) * mm});
            skLineSegment(sketch, "E90.MirrorCS", {"start": v(-15, -108) * mm, "end": v(-15, -120) * mm});
            skLineSegment(sketch, "E91.MirrorCS", {"start": v(-33, -90) * mm, "end": v(-15, -108) * mm});
            skLineSegment(sketch, "E92.MirrorCS", {"start": v(0, -90) * mm, "end": v(0, -120) * mm, "construction": true});
            skCircle(sketch, "E93.MirrorC", {"center": v(0, -120) * mm, "radius": 6 * mm});
            skSolve(sketch);
        }
        {
            var Q0;
            Q0=makeQuery(id+"F16.imprint","IMPRINT",FACE,{"disambiguationData":[TD([[makeQuery(id+"F16.imprint","IMPRINT",EDGE,{"derivedFrom":sQuery(id+"F16.wireOp",EDGE,"E80")}),-1.0]])]});
            var Q1;
            {var subQ0=sQuery(id+"F16.wireOp",EDGE,"E87.MirrorCS");Q1=makeQuery(id+"F16.imprint","IMPRINT",FACE,{"disambiguationData":[TD([[makeQuery(id+"F16.imprint","IMPRINT",EDGE,{"derivedFrom":subQ0}),-1.0]])]});}
            var Q2;
            Q2=makeQuery(id+"F16.imprint","IMPRINT",FACE,{"disambiguationData":[TD([[makeQuery(id+"F16.imprint","IMPRINT",EDGE,{"derivedFrom":makeQuery(id+"F1.opExtrude","CAP_EDGE",EDGE,{"disambiguationData":[OSD([sQuery(id+"F0.wireOp",EDGE,"E1.left")])],"isStart":true})}),-1.0]])]});
            var Q3;
            Q3=makeQuery(id+"F2.opExtrude","CAP_FACE",FACE,{"disambiguationData":[OSD([sQuery(id+"F0.wireOp",EDGE,"E12"),sQuery(id+"F0.wireOp",EDGE,"E13"),sQuery(id+"F0.wireOp",EDGE,"E14"),sQuery(id+"F0.wireOp",EDGE,"E15"),sQuery(id+"F0.wireOp",EDGE,"E17.filletArc"),sQuery(id+"F0.wireOp",EDGE,"E18.filletArc"),sQuery(id+"F0.wireOp",EDGE,"E19.filletArc"),sQuery(id+"F0.wireOp",EDGE,"E20.filletArc"),sQuery(id+"F0.wireOp",EDGE,"E25.0"),sQuery(id+"F0.wireOp",EDGE,"E25.1"),sQuery(id+"F0.wireOp",EDGE,"E25.2"),sQuery(id+"F0.wireOp",EDGE,"E25.3"),sQuery(id+"F0.wireOp",EDGE,"E25.4"),sQuery(id+"F0.wireOp",EDGE,"E25.5"),sQuery(id+"F0.wireOp",EDGE,"E25.6"),sQuery(id+"F0.wireOp",EDGE,"E25.7")])],"isStart":false});
            extrude(context, id + "F17", {"entities" : qUnion([Q0, Q1, Q2]), "endBound" : BoundingType.UP_TO_SURFACE, "depth" : 25 * mm, "endBoundEntityFace" : qUnion([Q3]), "offsetDistance" : 25 * mm});
        }
    });
